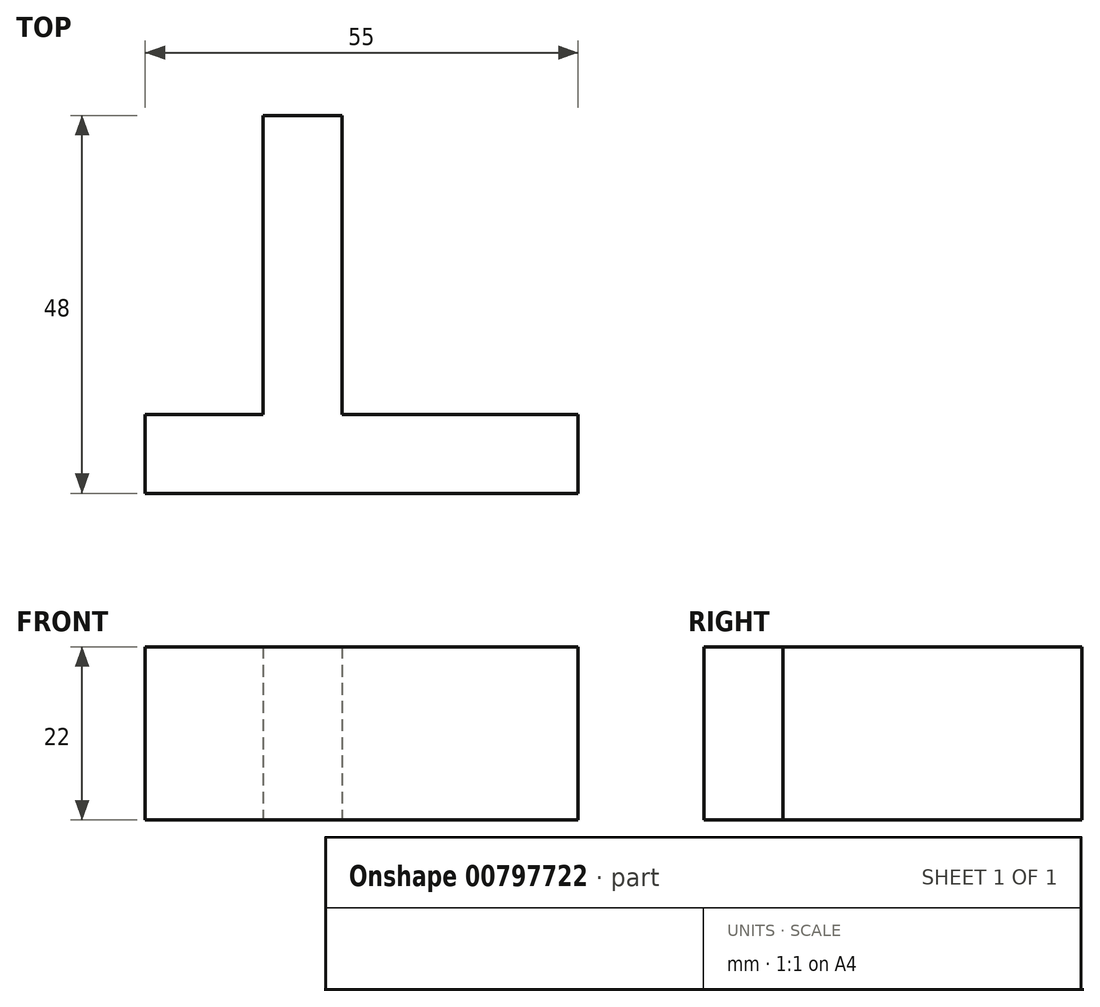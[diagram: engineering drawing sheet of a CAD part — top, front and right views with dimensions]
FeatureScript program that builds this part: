
annotation { "Feature Type Name" : "Feature", "Feature Type Description" : "" }
export const myFeature = defineFeature(function(context is Context, id is Id, definition is map)
    precondition{}
    {
        {
            var Q0;
            Q0=qCreatedBy(makeId("Top.planeOp"),FACE);
            var sketch = newSketch(context, id + "F0", { "sketchPlane" : qUnion([Q0])});
            skLineSegment(sketch, "E0.bottom", {"start": v(35, 5) * mm, "end": v(-20, 5) * mm});
            skLineSegment(sketch, "E0.top", {"start": v(35, -5) * mm, "end": v(-20, -5) * mm});
            skLineSegment(sketch, "E0.left", {"start": v(35, 5) * mm, "end": v(35, -5) * mm});
            skLineSegment(sketch, "E0.right", {"start": v(-20, 5) * mm, "end": v(-20, -5) * mm});
            skPoint(sketch, "E0.middle", {"position": v(0, 0) * mm});
            skLineSegment(sketch, "E1.bottom", {"start": v(5, 43) * mm, "end": v(-5, 43) * mm});
            skLineSegment(sketch, "E1.top", {"start": v(5, 5) * mm, "end": v(-5, 5) * mm});
            skLineSegment(sketch, "E1.left", {"start": v(5, 43) * mm, "end": v(5, 5) * mm});
            skLineSegment(sketch, "E1.right", {"start": v(-5, 43) * mm, "end": v(-5, 5) * mm});
            skPoint(sketch, "E1.middle", {"position": v(0, 24) * mm});
            skSolve(sketch);
        }
        {
            var Q0;
            Q0=makeQuery(id+"F0.imprint","IMPRINT",FACE,{"disambiguationData":[TD([[makeQuery(id+"F0.imprint","IMPRINT",EDGE,{"derivedFrom":sQuery(id+"F0.wireOp",EDGE,"E0.top")}),-1.0]])]});
            var Q1;
            Q1=makeQuery(id+"F0.imprint","IMPRINT",FACE,{"disambiguationData":[TD([[makeQuery(id+"F0.imprint","IMPRINT",EDGE,{"derivedFrom":sQuery(id+"F0.wireOp",EDGE,"E1.bottom")}),1.0]])]});
            extrude(context, id + "F1", {"entities" : qUnion([Q0, Q1]), "depth" : 22 * mm, "offsetDistance" : 25 * mm});
        }
    });
